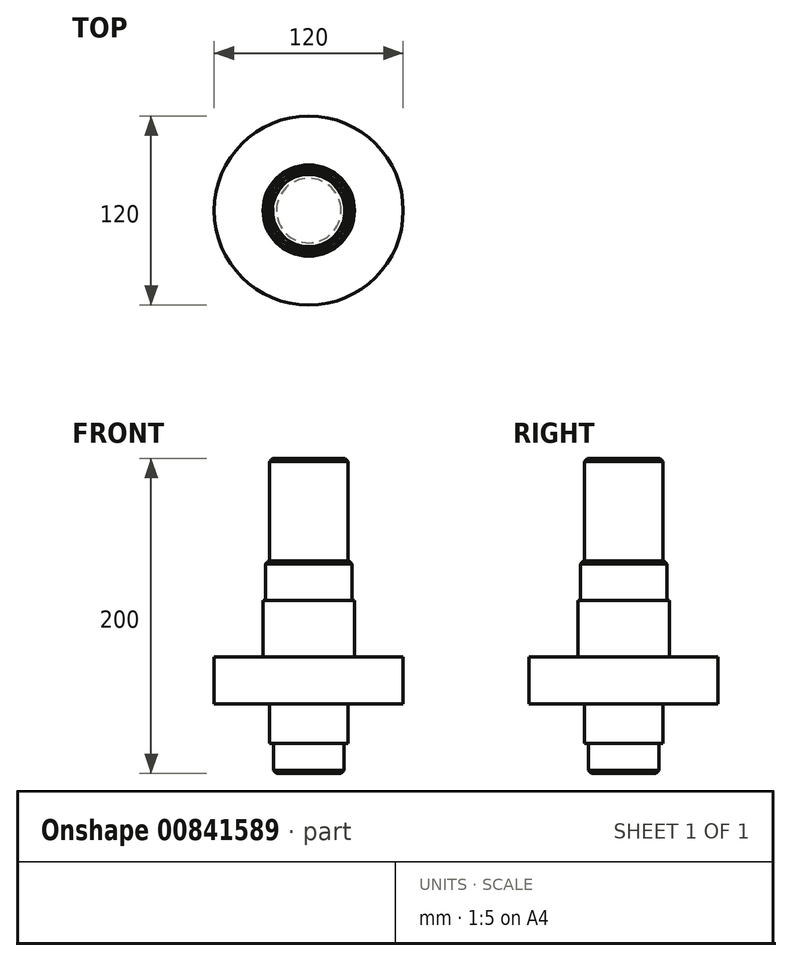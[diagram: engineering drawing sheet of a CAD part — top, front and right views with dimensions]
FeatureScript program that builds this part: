
annotation { "Feature Type Name" : "Feature", "Feature Type Description" : "" }
export const myFeature = defineFeature(function(context is Context, id is Id, definition is map)
    precondition{}
    {
        {
            var Q0;
            Q0=qCreatedBy(makeId("Front.planeOp"),FACE);
            var sketch = newSketch(context, id + "F0", { "sketchPlane" : qUnion([Q0])});
            skLineSegment(sketch, "E0", {"start": v(0, 0) * mm, "end": v(0, 200) * mm});
            skLineSegment(sketch, "E1", {"start": v(0, 0) * mm, "end": v(-22.5, 0) * mm});
            skLineSegment(sketch, "E2", {"start": v(-22.5, 0) * mm, "end": v(-22.5, 19) * mm});
            skLineSegment(sketch, "E3", {"start": v(-25, 19) * mm, "end": v(-22.5, 19) * mm});
            skLineSegment(sketch, "E4", {"start": v(-25, 19) * mm, "end": v(-25, 44) * mm});
            skLineSegment(sketch, "E5", {"start": v(-25, 44) * mm, "end": v(-60, 44) * mm});
            skLineSegment(sketch, "E6", {"start": v(-60, 44) * mm, "end": v(-60, 74) * mm});
            skLineSegment(sketch, "E7", {"start": v(-60, 74) * mm, "end": v(-29, 74) * mm});
            skLineSegment(sketch, "E8", {"start": v(-29, 74) * mm, "end": v(-29, 110) * mm});
            skLineSegment(sketch, "E9", {"start": v(-25, 200) * mm, "end": v(0, 200) * mm});
            skLineSegment(sketch, "E10", {"start": v(0, 200) * mm, "end": v(0, -17.45) * mm, "construction": true});
            skLineSegment(sketch, "E11", {"start": v(-29, 110) * mm, "end": v(-27.5, 110) * mm});
            skLineSegment(sketch, "E12", {"start": v(-27.5, 110) * mm, "end": v(-27.5, 135) * mm});
            skPoint(sketch, "E13.orphan", {"position": v(-22.5, 200) * mm});
            skLineSegment(sketch, "E14", {"start": v(-27.5, 135) * mm, "end": v(-25, 135) * mm});
            skLineSegment(sketch, "E15", {"start": v(-25, 135) * mm, "end": v(-25, 200) * mm});
            skSolve(sketch);
        }
        {
            var Q0;
            Q0 = qSketchRegion(id + "F0", true);
            var Q1;
            Q1=sQuery(id+"F0.wireOp",EDGE,"E10");
            revolve(context, id + "F1", {"surfaceOperationType" : NewSurfaceOperationType.NEW, "entities" : qUnion([Q0]), "axis" : qUnion([Q1]), "revolveType" : RevolveType.FULL});
        }
        {
            var Q0;
            Q0=makeQuery(id+"F1.opRevolve","SWEPT_EDGE",EDGE,{"disambiguationData":[OSD([sQuery(id+"F0.wireOp",EDGE,"E1"),sQuery(id+"F0.wireOp",EDGE,"E2")])]});
            var Q1;
            Q1=makeQuery(id+"F1.opRevolve","SWEPT_EDGE",EDGE,{"disambiguationData":[OSD([sQuery(id+"F0.wireOp",EDGE,"E9"),sQuery(id+"F0.wireOp",EDGE,"E15")])]});
            var Q2;
            Q2=makeQuery(id+"F1.opRevolve","SWEPT_EDGE",EDGE,{"disambiguationData":[OSD([sQuery(id+"F0.wireOp",EDGE,"E12"),sQuery(id+"F0.wireOp",EDGE,"E14")])]});
            chamfer(context, id + "F2", {"entities" : qUnion([Q0, Q1, Q2]), "width" : 2 * mm, "tangentPropagation" : true});
        }
    });
